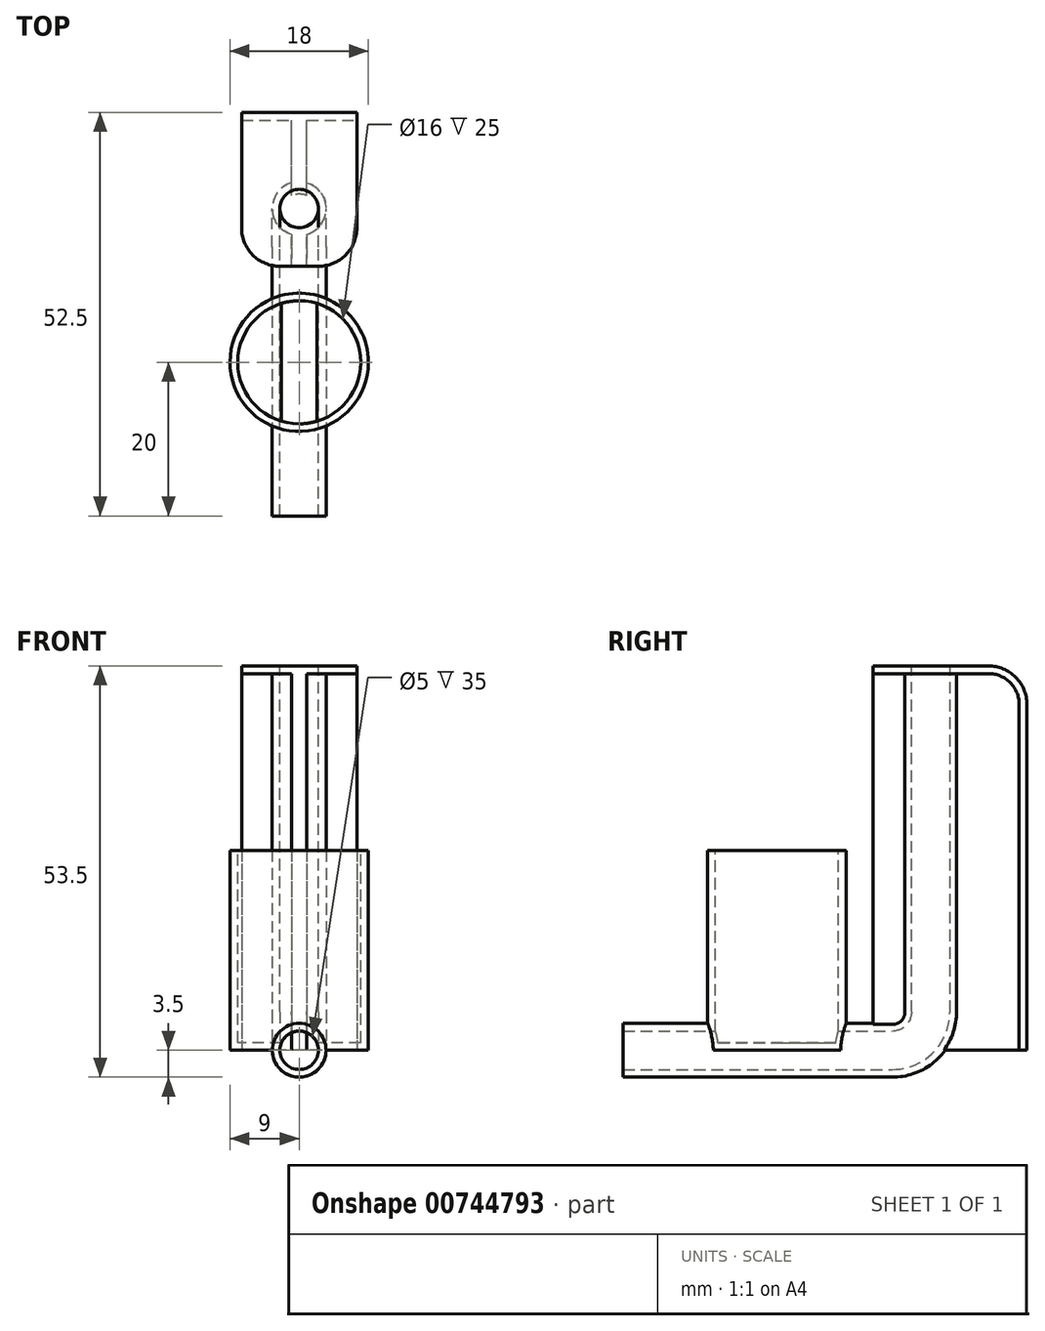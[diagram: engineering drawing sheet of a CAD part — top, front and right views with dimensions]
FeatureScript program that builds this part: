
annotation { "Feature Type Name" : "Feature", "Feature Type Description" : "" }
export const myFeature = defineFeature(function(context is Context, id is Id, definition is map)
    precondition{}
    {
        {
            var Q0;
            Q0=qCreatedBy(makeId("Top.planeOp"),FACE);
            var sketch = newSketch(context, id + "F0", { "sketchPlane" : qUnion([Q0])});
            skCircle(sketch, "E0", {"center": v(0, 0) * mm, "radius": 9 * mm});
            skSolve(sketch);
        }
        {
            var Q0;
            Q0=makeQuery(id+"F0.imprint","IMPRINT",FACE,{"disambiguationData":[TD([[makeQuery(id+"F0.imprint","IMPRINT",EDGE,{"derivedFrom":sQuery(id+"F0.wireOp",EDGE,"E0")}),1.0]])]});
            extrude(context, id + "F1", {"entities" : qUnion([Q0]), "depth" : 26 * mm, "offsetDistance" : 25 * mm});
        }
        {
            var Q0;
            Q0=qCreatedBy(makeId("Right.planeOp"),FACE);
            var sketch = newSketch(context, id + "F2", { "sketchPlane" : qUnion([Q0])});
            skLineSegment(sketch, "E1.right", {"start": v(32.5, 0) * mm, "end": v(32.5, 45) * mm});
            skPoint(sketch, "E2.visualSharp", {"position": v(32.5, 50) * mm});
            skArc(sketch, "E2.filletArc", {"start": v(32.5, 45) * mm, "mid": v(31.04, 48.54) * mm, "end": v(27.5, 50) * mm});
            skLineSegment(sketch, "E3", {"start": v(12.5, 50) * mm, "end": v(12.5, 0) * mm});
            skLineSegment(sketch, "E4", {"start": v(12.5, 50) * mm, "end": v(27.5, 50) * mm});
            skLineSegment(sketch, "E5", {"start": v(12.5, 0) * mm, "end": v(32.5, 0) * mm});
            skSolve(sketch);
        }
        {
            var Q0;
            Q0 = qSketchRegion(id + "F2", true);
            extrude(context, id + "F3", {"entities" : qUnion([Q0]), "endBound" : BoundingType.SYMMETRIC, "depth" : 2 * mm, "offsetDistance" : 25 * mm});
        }
        {
            var Q0;
            Q0=qCreatedBy(makeId("Front.planeOp"),FACE);
            var sketch = newSketch(context, id + "F4", { "sketchPlane" : qUnion([Q0])});
            skCircle(sketch, "E6", {"center": v(0, 0) * mm, "radius": 3.5 * mm});
            skSolve(sketch);
        }
        {
            var Q0;
            Q0=qCreatedBy(makeId("Right.planeOp"),FACE);
            var sketch = newSketch(context, id + "F5", { "sketchPlane" : qUnion([Q0])});
            skLineSegment(sketch, "E7", {"start": v(0, 0) * mm, "end": v(15, 0) * mm});
            skLineSegment(sketch, "E8", {"start": v(20, 5) * mm, "end": v(20, 50) * mm});
            skLineSegment(sketch, "E9", {"start": v(0, 0) * mm, "end": v(-20, 0) * mm});
            skPoint(sketch, "E10.visualSharp", {"position": v(20, 0) * mm});
            skArc(sketch, "E10.filletArc", {"start": v(15, 0) * mm, "mid": v(18.54, 1.46) * mm, "end": v(20, 5) * mm});
            skSolve(sketch);
        }
        {
            var Q0;
            Q0 = qSketchRegion(id + "F4", true);
            var Q1;
            Q1 = qConstructionFilter(qBodyType(qCreatedBy(id + "F5" ,EDGE), BodyType.WIRE), ConstructionObject.NO);
            sweep(context, id + "F6", {"operationType" : NewBodyOperationType.ADD, "profiles" : qUnion([Q0]), "path" : qUnion([Q1])});
        }
        {
            var Q0;
            Q0=makeQuery(id+"F6.opSweep","CAP_FACE",FACE,{"disambiguationData":[OSD([sQuery(id+"F4.wireOp",EDGE,"E6"),sQuery(id+"F5.wireOp",VERTEX,"E9.end")])],"isStart":false});
            var sketch = newSketch(context, id + "F7", { "sketchPlane" : qUnion([Q0])});
            skCircle(sketch, "E11", {"center": v(0, 0) * mm, "radius": 2.5 * mm});
            skSolve(sketch);
        }
        {
            var Q0;
            Q0 = qSketchRegion(id + "F7", true);
            var Q1;
            Q1 = qConstructionFilter(qBodyType(qCreatedBy(id + "F5" ,EDGE), BodyType.WIRE), ConstructionObject.NO);
            sweep(context, id + "F8", {"operationType" : NewBodyOperationType.REMOVE, "profiles" : qUnion([Q0]), "path" : qUnion([Q1])});
        }
        {
            var Q0;
            Q0=makeQuery(id+"F1.opExtrude","CAP_FACE",FACE,{"disambiguationData":[OSD([sQuery(id+"F0.wireOp",EDGE,"E0")])],"isStart":false});
            var sketch = newSketch(context, id + "F9", { "sketchPlane" : qUnion([Q0])});
            skCircle(sketch, "E12", {"center": v(0, 0) * mm, "radius": 8 * mm});
            skSolve(sketch);
        }
        {
            var Q0;
            Q0=makeQuery(id+"F9.imprint","IMPRINT",FACE,{"disambiguationData":[TD([[makeQuery(id+"F9.imprint","IMPRINT",EDGE,{"derivedFrom":sQuery(id+"F9.wireOp",EDGE,"E12")}),1.0]])]});
            extrude(context, id + "F10", {"entities" : qUnion([Q0]), "operationType" : NewBodyOperationType.REMOVE, "oppositeDirection" : true, "depth" : 25 * mm, "offsetDistance" : 25 * mm});
        }
        {
            var Q0;
            Q0=makeQuery(id+"F6.boolean.opBoolean","MERGE",FACE,{"derivedFrom":[makeQuery(id+"F3.opExtrude","SWEPT_FACE",FACE,{"disambiguationData":[OSD([sQuery(id+"F2.wireOp",EDGE,"E4")])]}),makeQuery(id+"F6.opSweep","CAP_FACE",FACE,{"disambiguationData":[OSD([sQuery(id+"F4.wireOp",EDGE,"E6"),sQuery(id+"F5.wireOp",VERTEX,"E8.end")])],"isStart":true})]});
            var sketch = newSketch(context, id + "F11", { "sketchPlane" : qUnion([Q0])});
            skSolve(sketch);
        }
        {
            var Q0;
            {var subQ0=sQuery(id+"F2.wireOp",EDGE,"E4");var subQ8=sQuery(id+"F2.wireOp",EDGE,"E2.filletArc");Q0=makeQuery(id+"F11.imprint","IMPRINT",FACE,{"disambiguationData":[TD([[makeQuery(id+"F11.imprint","IMPRINT",EDGE,{"derivedFrom":makeQuery(id+"F3.opExtrude","SWEPT_EDGE",EDGE,{"disambiguationData":[OSD([subQ8,subQ0])]})}),1.0]])]});}
            var sketch = newSketch(context, id + "F12", { "sketchPlane" : qUnion([Q0])});
            skLineSegment(sketch, "E13.bottom", {"start": v(-7.5, 25) * mm, "end": v(7.5, 25) * mm});
            skLineSegment(sketch, "E13.top", {"start": v(-2.5, 12.5) * mm, "end": v(2.5, 12.5) * mm});
            skLineSegment(sketch, "E13.left", {"start": v(-7.5, 25) * mm, "end": v(-7.5, 17.5) * mm});
            skLineSegment(sketch, "E13.right", {"start": v(7.5, 25) * mm, "end": v(7.5, 17.5) * mm});
            skPoint(sketch, "E14.visualSharp", {"position": v(-7.5, 12.5) * mm});
            skArc(sketch, "E14.filletArc", {"start": v(-7.5, 17.5) * mm, "mid": v(-6.04, 13.96) * mm, "end": v(-2.5, 12.5) * mm});
            skPoint(sketch, "E15.visualSharp", {"position": v(7.5, 12.5) * mm});
            skArc(sketch, "E15.filletArc", {"start": v(2.5, 12.5) * mm, "mid": v(6.04, 13.96) * mm, "end": v(7.5, 17.5) * mm});
            skSolve(sketch);
        }
        {
            var Q0;
            {var subQ13=sQuery(id+"F12.wireOp",EDGE,"E13.right");Q0=makeQuery(id+"F12.imprint","IMPRINT",FACE,{"disambiguationData":[TD([[makeQuery(id+"F12.imprint","IMPRINT",EDGE,{"derivedFrom":subQ13}),-1.0]])]});}
            var Q1;
            {var subQ0=sQuery(id+"F12.wireOp",EDGE,"E13.left");Q1=makeQuery(id+"F12.imprint","IMPRINT",FACE,{"disambiguationData":[TD([[makeQuery(id+"F12.imprint","IMPRINT",EDGE,{"derivedFrom":subQ0}),1.0]])]});}
            extrude(context, id + "F13", {"entities" : qUnion([Q0, Q1]), "operationType" : NewBodyOperationType.ADD, "oppositeDirection" : true, "depth" : 1 * mm, "offsetDistance" : 25 * mm});
        }
        {
            var Q0;
            {var subQ0=sQuery(id+"F12.wireOp",EDGE,"E13.bottom");Q0=makeQuery(id+"F13.opExtrude","SWEPT_FACE",FACE,{"disambiguationData":[OSD([subQ0]),TDD([makeQuery(id+"F12.imprint","IMPRINT",EDGE,{"disambiguationData":[TD([[makeQuery(id+"F12.imprint","INTERSECT",VERTEX,{"derivedFrom":[subQ0,sQuery(id+"F12.wireOp",EDGE,"E13.right")]}),1.0]])],"derivedFrom":subQ0})])]});}
            var Q1;
            {var subQ0=sQuery(id+"F12.wireOp",EDGE,"E13.bottom");Q1=makeQuery(id+"F13.opExtrude","SWEPT_FACE",FACE,{"disambiguationData":[OSD([subQ0]),TDD([makeQuery(id+"F12.imprint","IMPRINT",EDGE,{"disambiguationData":[TD([[makeQuery(id+"F12.imprint","INTERSECT",VERTEX,{"derivedFrom":[subQ0,sQuery(id+"F12.wireOp",EDGE,"E13.left")]}),-1.0]])],"derivedFrom":subQ0})])]});}
            var Q2;
            {var subQ1=sQuery(id+"F2.wireOp",EDGE,"E4");var subQ2=sQuery(id+"F2.wireOp",EDGE,"E2.filletArc");Q2=makeQuery(id+"F6.boolean.opBoolean","SPLIT",EDGE,{"disambiguationData":[TD([makeQuery(id+"F3.opExtrude","SWEPT_FACE",FACE,{"disambiguationData":[OSD([subQ2])]})])],"derivedFrom":makeQuery(id+"F3.opExtrude","CAP_EDGE",EDGE,{"disambiguationData":[OSD([subQ1])],"isStart":false})});}
            var Q3;
            Q3=makeQuery(id+"F3.opExtrude","CAP_EDGE",EDGE,{"disambiguationData":[OSD([sQuery(id+"F2.wireOp",EDGE,"E2.filletArc")])],"isStart":false});
            var Q4;
            Q4=makeQuery(id+"F3.opExtrude","CAP_EDGE",EDGE,{"disambiguationData":[OSD([sQuery(id+"F2.wireOp",EDGE,"E1.right")])],"isStart":false});
            sweep(context, id + "F14", {"operationType" : NewBodyOperationType.ADD, "profiles" : qUnion([Q0, Q1]), "path" : qUnion([Q2, Q3, Q4])});
        }
    });
